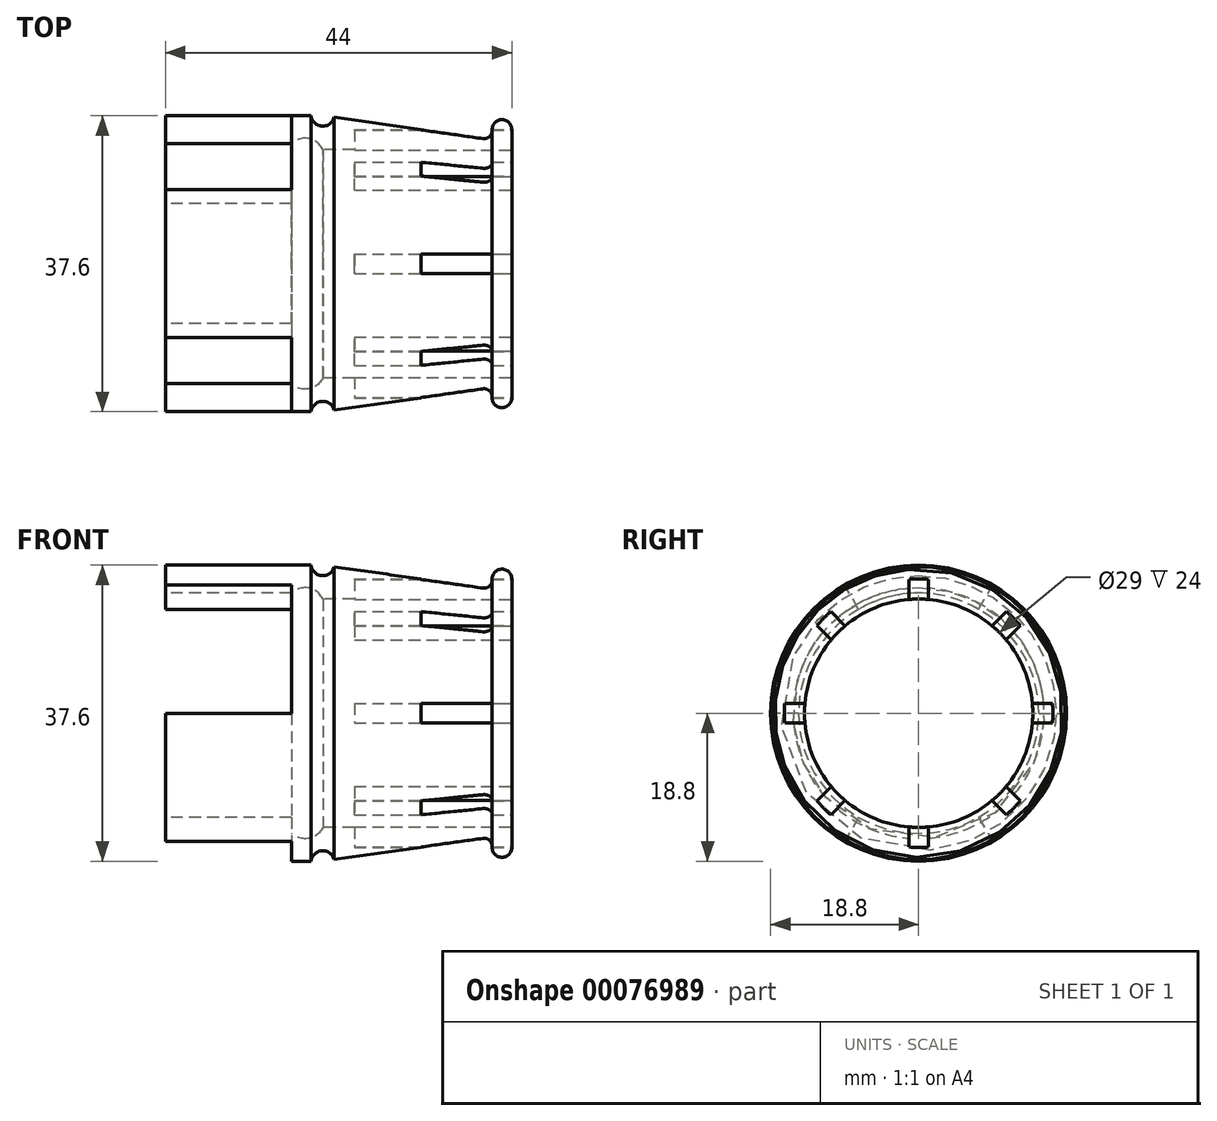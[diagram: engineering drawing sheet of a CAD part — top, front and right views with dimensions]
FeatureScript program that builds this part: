
annotation { "Feature Type Name" : "Feature", "Feature Type Description" : "" }
export const myFeature = defineFeature(function(context is Context, id is Id, definition is map)
    precondition{}
    {
        {
            var Q0;
            Q0=qCreatedBy(makeId("Front.planeOp"),FACE);
            var sketch = newSketch(context, id + "F0", { "sketchPlane" : qUnion([Q0])});
            skLineSegment(sketch, "E0.bottom", {"start": v(0, 14.5) * mm, "end": v(24, 14.5) * mm});
            skLineSegment(sketch, "E0.top", {"start": v(-20, 0) * mm, "end": v(24, 0) * mm});
            skLineSegment(sketch, "E0.left", {"start": v(-20, 14.5) * mm, "end": v(-20, 0) * mm});
            skLineSegment(sketch, "E0.right", {"start": v(24, 14.5) * mm, "end": v(24, 0) * mm});
            skLineSegment(sketch, "E1.top", {"start": v(-20, 18.8) * mm, "end": v(-1.5, 18.8) * mm});
            skLineSegment(sketch, "E1.left", {"start": v(-20, 14.5) * mm, "end": v(-20, 18.8) * mm});
            skLineSegment(sketch, "E1.right", {"start": v(24, 13.25) * mm, "end": v(24, 14.5) * mm});
            skLineSegment(sketch, "E2.bottom", {"start": v(-20, 15.25) * mm, "end": v(-4, 15.25) * mm});
            skLineSegment(sketch, "E2.left", {"start": v(-20, 15.25) * mm, "end": v(-20, 0) * mm});
            skLineSegment(sketch, "E2.right", {"start": v(0, 15.25) * mm, "end": v(0, 0) * mm});
            skLineSegment(sketch, "E3", {"start": v(0, 15.25) * mm, "end": v(0, 14.5) * mm});
            skLineSegment(sketch, "E4", {"start": v(0, 18.8) * mm, "end": v(0, -19.5) * mm, "construction": true});
            skLineSegment(sketch, "E5", {"start": v(1.44, 18.6) * mm, "end": v(20.36, 15.94) * mm});
            skPoint(sketch, "E6.orphan", {"position": v(24, 18.8) * mm});
            skLineSegment(sketch, "E7", {"start": v(-4, 18.8) * mm, "end": v(-4, 0) * mm});
            skLineSegment(sketch, "E8", {"start": v(24, 13.25) * mm, "end": v(24, 17.05) * mm});
            skLineSegment(sketch, "E9", {"start": v(22.75, 18.3) * mm, "end": v(22.75, 18.3) * mm});
            skLineSegment(sketch, "E10", {"start": v(21.5, 17.05) * mm, "end": v(21.5, 16.93) * mm});
            skArc(sketch, "E11.filletArc", {"start": v(20.36, 15.94) * mm, "mid": v(21.16, 16.17) * mm, "end": v(21.5, 16.93) * mm});
            skPoint(sketch, "E12.visualSharp", {"position": v(21.5, 18.3) * mm});
            skArc(sketch, "E12.filletArc", {"start": v(22.75, 18.3) * mm, "mid": v(21.87, 17.93) * mm, "end": v(21.5, 17.05) * mm});
            skPoint(sketch, "E13.visualSharp", {"position": v(24, 18.3) * mm});
            skArc(sketch, "E13.filletArc", {"start": v(24, 17.05) * mm, "mid": v(23.63, 17.93) * mm, "end": v(22.75, 18.3) * mm});
            skArc(sketch, "E14", {"start": v(-1.5, 18.8) * mm, "mid": v(-0.12, 17.48) * mm, "end": v(1.44, 18.6) * mm});
            skPoint(sketch, "E15.orphan", {"position": v(0, -15.25) * mm});
            skArc(sketch, "E16", {"start": v(0, 14.5) * mm, "mid": v(-1.8, 15.9) * mm, "end": v(-4, 15.25) * mm});
            skSolve(sketch);
        }
        {
            var Q0;
            {var subQ0=sQuery(id+"F0.wireOp",EDGE,"E1.left");Q0=makeQuery(id+"F0.imprint","IMPRINT",FACE,{"disambiguationData":[TD([[makeQuery(id+"F0.imprint","IMPRINT",EDGE,{"derivedFrom":subQ0}),-1.0]])]});}
            var Q1;
            {var subQ0=sQuery(id+"F0.wireOp",EDGE,"E1.right");Q1=makeQuery(id+"F0.imprint","IMPRINT",FACE,{"disambiguationData":[TD([[makeQuery(id+"F0.imprint","IMPRINT",EDGE,{"derivedFrom":subQ0}),1.0]])]});}
            var Q2;
            Q2=makeQuery(id+"F0.imprint","IMPRINT",FACE,{"disambiguationData":[TD([[makeQuery(id+"F0.imprint","IMPRINT",EDGE,{"derivedFrom":sQuery(id+"F0.wireOp",EDGE,"E5")}),-1.0]])]});
            var Q3;
            Q3=sQuery(id+"F0.wireOp",EDGE,"E0.top");
            revolve(context, id + "F1", {"entities" : qUnion([Q0, Q1, Q2]), "axis" : qUnion([Q3]), "revolveType" : RevolveType.FULL});
        }
        {
            var Q0;
            Q0=makeQuery(id+"F1.opRevolve","SWEPT_FACE",FACE,{"disambiguationData":[OSD([sQuery(id+"F0.wireOp",EDGE,"E1.left")])]});
            var sketch = newSketch(context, id + "F2", { "sketchPlane" : qUnion([Q0])});
            skCircle(sketch, "E17.0", {"center": v(0, 0) * mm, "radius": 15.25 * mm});
            skCircle(sketch, "E18.0", {"center": v(0, 0) * mm, "radius": 18.8 * mm});
            skLineSegment(sketch, "E19", {"start": v(0, 0) * mm, "end": v(-9.4, 16.28) * mm});
            skLineSegment(sketch, "E20", {"start": v(0, 0) * mm, "end": v(-18.8, 0) * mm});
            skLineSegment(sketch, "E21", {"start": v(0, 0) * mm, "end": v(9.4, 16.28) * mm});
            skLineSegment(sketch, "E22", {"start": v(0, 0) * mm, "end": v(18.8, 0) * mm});
            skLineSegment(sketch, "E23", {"start": v(0, 0) * mm, "end": v(9.4, -16.28) * mm});
            skLineSegment(sketch, "E24", {"start": v(0, 0) * mm, "end": v(-9.4, -16.28) * mm});
            skSolve(sketch);
        }
        {
            var Q0;
            {var subQ0=sQuery(id+"F2.wireOp",EDGE,"E20");var subQ1=sQuery(id+"F2.wireOp",EDGE,"E17.0");var subQ2=makeQuery(id+"F2.imprint","INTERSECT",VERTEX,{"derivedFrom":[subQ1,subQ0]});Q0=makeQuery(id+"F2.imprint","IMPRINT",FACE,{"disambiguationData":[TD([[makeQuery(id+"F2.imprint","IMPRINT",EDGE,{"disambiguationData":[TD([[subQ2,1.0]])],"derivedFrom":subQ1}),-1.0]])]});}
            var Q1;
            {var subQ0=sQuery(id+"F2.wireOp",EDGE,"E22");var subQ1=sQuery(id+"F2.wireOp",EDGE,"E17.0");var subQ2=makeQuery(id+"F2.imprint","INTERSECT",VERTEX,{"derivedFrom":[subQ1,subQ0]});Q1=makeQuery(id+"F2.imprint","IMPRINT",FACE,{"disambiguationData":[TD([[makeQuery(id+"F2.imprint","IMPRINT",EDGE,{"disambiguationData":[TD([[subQ2,-1.0]])],"derivedFrom":subQ1}),-1.0]])]});}
            var Q2;
            {var subQ0=sQuery(id+"F2.wireOp",EDGE,"E24");var subQ1=sQuery(id+"F2.wireOp",EDGE,"E17.0");var subQ2=makeQuery(id+"F2.imprint","INTERSECT",VERTEX,{"derivedFrom":[subQ1,subQ0]});Q2=makeQuery(id+"F2.imprint","IMPRINT",FACE,{"disambiguationData":[TD([[makeQuery(id+"F2.imprint","IMPRINT",EDGE,{"disambiguationData":[TD([[subQ2,-1.0]])],"derivedFrom":subQ1}),-1.0]])]});}
            extrude(context, id + "F3", {"entities" : qUnion([Q0, Q1, Q2]), "operationType" : NewBodyOperationType.REMOVE, "oppositeDirection" : true, "depth" : 16 * mm});
        }
        {
            var Q0;
            Q0=makeQuery(id+"F1.opRevolve","SWEPT_FACE",FACE,{"disambiguationData":[OSD([sQuery(id+"F0.wireOp",EDGE,"E8")])]});
            var sketch = newSketch(context, id + "F4", { "sketchPlane" : qUnion([Q0])});
            skCircle(sketch, "E25.0", {"center": v(0, 0) * mm, "radius": 14.5 * mm, "construction": true});
            skCircle(sketch, "E26.0", {"center": v(0, 0) * mm, "radius": 17.05 * mm, "construction": true});
            skCircle(sketch, "E27.0", {"center": v(0, 0) * mm, "radius": 18.8 * mm, "construction": true});
            skLineSegment(sketch, "E28", {"start": v(0, 21) * mm, "end": v(0, -20.6) * mm, "construction": true});
            skLineSegment(sketch, "E29", {"start": v(22.7, 0) * mm, "end": v(-23.6, 0) * mm, "construction": true});
            skLineSegment(sketch, "E30", {"start": v(-17.5, 17.5) * mm, "end": v(0, 0) * mm, "construction": true});
            skLineSegment(sketch, "E31", {"start": v(0, 0) * mm, "end": v(17.06, -17.06) * mm, "construction": true});
            skLineSegment(sketch, "E32", {"start": v(0, 0) * mm, "end": v(14.47, 14.47) * mm, "construction": true});
            skLineSegment(sketch, "E33", {"start": v(0, 0) * mm, "end": v(-15.58, -15.58) * mm, "construction": true});
            skArc(sketch, "E34.0.startCap", {"start": v(-18.39, 16.62) * mm, "mid": v(-18.39, 18.39) * mm, "end": v(-16.62, 18.39) * mm});
            skArc(sketch, "E34.0.endCap", {"start": v(0.88, 0.88) * mm, "mid": v(0.88, -0.88) * mm, "end": v(-0.88, -0.88) * mm});
            skLineSegment(sketch, "E34.0.left", {"start": v(-16.62, 18.39) * mm, "end": v(0.88, 0.88) * mm});
            skLineSegment(sketch, "E34.0.right", {"start": v(-18.39, 16.62) * mm, "end": v(-0.88, -0.88) * mm});
            skArc(sketch, "E35.0.startCap", {"start": v(-1.25, 21) * mm, "mid": v(0, 22.25) * mm, "end": v(1.25, 21) * mm});
            skArc(sketch, "E35.0.endCap", {"start": v(1.25, -20.6) * mm, "mid": v(0, -21.85) * mm, "end": v(-1.25, -20.6) * mm});
            skLineSegment(sketch, "E35.0.left", {"start": v(1.25, 21) * mm, "end": v(1.25, -20.6) * mm});
            skLineSegment(sketch, "E35.0.right", {"start": v(-1.25, 21) * mm, "end": v(-1.25, -20.6) * mm});
            skArc(sketch, "E36.0.startCap", {"start": v(0.88, -0.88) * mm, "mid": v(-0.88, -0.88) * mm, "end": v(-0.88, 0.88) * mm});
            skArc(sketch, "E36.0.endCap", {"start": v(13.58, 15.35) * mm, "mid": v(15.35, 15.35) * mm, "end": v(15.35, 13.58) * mm});
            skLineSegment(sketch, "E36.0.left", {"start": v(-0.88, 0.88) * mm, "end": v(13.58, 15.35) * mm});
            skLineSegment(sketch, "E36.0.right", {"start": v(0.88, -0.88) * mm, "end": v(15.35, 13.58) * mm});
            skArc(sketch, "E36.1.startCap", {"start": v(-0.88, 0.88) * mm, "mid": v(0.88, 0.88) * mm, "end": v(0.88, -0.88) * mm});
            skArc(sketch, "E36.1.endCap", {"start": v(-14.7, -16.46) * mm, "mid": v(-16.46, -16.46) * mm, "end": v(-16.46, -14.7) * mm});
            skLineSegment(sketch, "E36.1.left", {"start": v(0.88, -0.88) * mm, "end": v(-14.7, -16.46) * mm});
            skLineSegment(sketch, "E36.1.right", {"start": v(-0.88, 0.88) * mm, "end": v(-16.46, -14.7) * mm});
            skArc(sketch, "E36.2.startCap", {"start": v(22.7, 1.25) * mm, "mid": v(23.96, 0) * mm, "end": v(22.7, -1.25) * mm});
            skArc(sketch, "E36.2.endCap", {"start": v(-23.6, -1.25) * mm, "mid": v(-24.84, 0) * mm, "end": v(-23.6, 1.25) * mm});
            skLineSegment(sketch, "E36.2.left", {"start": v(22.7, -1.25) * mm, "end": v(-23.6, -1.25) * mm});
            skLineSegment(sketch, "E36.2.right", {"start": v(22.7, 1.25) * mm, "end": v(-23.6, 1.25) * mm});
            skArc(sketch, "E36.3.startCap", {"start": v(-0.88, -0.88) * mm, "mid": v(-0.88, 0.88) * mm, "end": v(0.88, 0.88) * mm});
            skArc(sketch, "E36.3.endCap", {"start": v(17.95, -16.18) * mm, "mid": v(17.95, -17.95) * mm, "end": v(16.18, -17.95) * mm});
            skLineSegment(sketch, "E36.3.left", {"start": v(0.88, 0.88) * mm, "end": v(17.95, -16.18) * mm});
            skLineSegment(sketch, "E36.3.right", {"start": v(-0.88, -0.88) * mm, "end": v(16.18, -17.95) * mm});
            skSolve(sketch);
        }
        {
            var Q0;
            {var subQ0=sQuery(id+"F4.wireOp",EDGE,"E34.0.left");var subQ1=sQuery(id+"F0.wireOp",EDGE,"E8");var subQ2=makeQuery(id+"F1.opRevolve","SWEPT_EDGE",EDGE,{"disambiguationData":[OSD([subQ1,sQuery(id+"F0.wireOp",EDGE,"E13.filletArc")])]});var subQ3=makeQuery(id+"F4.imprint","INTERSECT",VERTEX,{"derivedFrom":[subQ2,subQ0]});Q0=makeQuery(id+"F4.imprint","IMPRINT",FACE,{"disambiguationData":[TD([[makeQuery(id+"F4.imprint","IMPRINT",EDGE,{"disambiguationData":[TD([[subQ3,-1.0]])],"derivedFrom":subQ0}),-1.0]])]});}
            var Q1;
            {var subQ0=sQuery(id+"F4.wireOp",EDGE,"E34.0.startCap");Q1=makeQuery(id+"F4.imprint","IMPRINT",FACE,{"disambiguationData":[TD([[makeQuery(id+"F4.imprint","IMPRINT",EDGE,{"derivedFrom":subQ0}),-1.0]])]});}
            var Q2;
            {var subQ0=sQuery(id+"F4.wireOp",EDGE,"E35.0.left");var subQ1=sQuery(id+"F0.wireOp",EDGE,"E8");var subQ2=makeQuery(id+"F1.opRevolve","SWEPT_EDGE",EDGE,{"disambiguationData":[OSD([subQ1,sQuery(id+"F0.wireOp",EDGE,"E13.filletArc")])]});var subQ3=makeQuery(id+"F4.imprint","INTERSECT",VERTEX,{"disambiguationData":[OD(0.0)],"derivedFrom":[subQ2,subQ0]});Q2=makeQuery(id+"F4.imprint","IMPRINT",FACE,{"disambiguationData":[TD([[makeQuery(id+"F4.imprint","IMPRINT",EDGE,{"disambiguationData":[TD([[subQ3,-1.0]])],"derivedFrom":subQ0}),-1.0]])]});}
            var Q3;
            {var subQ0=sQuery(id+"F4.wireOp",EDGE,"E35.0.startCap");Q3=makeQuery(id+"F4.imprint","IMPRINT",FACE,{"disambiguationData":[TD([[makeQuery(id+"F4.imprint","IMPRINT",EDGE,{"derivedFrom":subQ0}),-1.0]])]});}
            var Q4;
            {var subQ0=sQuery(id+"F4.wireOp",EDGE,"E36.0.left");var subQ1=sQuery(id+"F0.wireOp",EDGE,"E8");var subQ2=makeQuery(id+"F1.opRevolve","SWEPT_EDGE",EDGE,{"disambiguationData":[OSD([subQ1,sQuery(id+"F0.wireOp",EDGE,"E13.filletArc")])]});var subQ3=makeQuery(id+"F4.imprint","INTERSECT",VERTEX,{"derivedFrom":[subQ2,subQ0]});Q4=makeQuery(id+"F4.imprint","IMPRINT",FACE,{"disambiguationData":[TD([[makeQuery(id+"F4.imprint","IMPRINT",EDGE,{"disambiguationData":[TD([[subQ3,1.0]])],"derivedFrom":subQ0}),-1.0]])]});}
            var Q5;
            {var subQ0=sQuery(id+"F4.wireOp",EDGE,"E36.0.endCap");Q5=makeQuery(id+"F4.imprint","IMPRINT",FACE,{"disambiguationData":[TD([[makeQuery(id+"F4.imprint","IMPRINT",EDGE,{"derivedFrom":subQ0}),-1.0]])]});}
            var Q6;
            {var subQ0=sQuery(id+"F4.wireOp",EDGE,"E36.2.left");var subQ1=sQuery(id+"F0.wireOp",EDGE,"E8");var subQ2=makeQuery(id+"F1.opRevolve","SWEPT_EDGE",EDGE,{"disambiguationData":[OSD([subQ1,sQuery(id+"F0.wireOp",EDGE,"E13.filletArc")])]});var subQ3=makeQuery(id+"F4.imprint","INTERSECT",VERTEX,{"disambiguationData":[OD(0.0)],"derivedFrom":[subQ2,subQ0]});Q6=makeQuery(id+"F4.imprint","IMPRINT",FACE,{"disambiguationData":[TD([[makeQuery(id+"F4.imprint","IMPRINT",EDGE,{"disambiguationData":[TD([[subQ3,-1.0]])],"derivedFrom":subQ0}),-1.0]])]});}
            var Q7;
            {var subQ0=sQuery(id+"F4.wireOp",EDGE,"E36.2.startCap");Q7=makeQuery(id+"F4.imprint","IMPRINT",FACE,{"disambiguationData":[TD([[makeQuery(id+"F4.imprint","IMPRINT",EDGE,{"derivedFrom":subQ0}),-1.0]])]});}
            var Q8;
            {var subQ0=sQuery(id+"F4.wireOp",EDGE,"E36.3.left");var subQ1=sQuery(id+"F0.wireOp",EDGE,"E8");var subQ2=makeQuery(id+"F1.opRevolve","SWEPT_EDGE",EDGE,{"disambiguationData":[OSD([subQ1,sQuery(id+"F0.wireOp",EDGE,"E13.filletArc")])]});var subQ3=makeQuery(id+"F4.imprint","INTERSECT",VERTEX,{"derivedFrom":[subQ2,subQ0]});Q8=makeQuery(id+"F4.imprint","IMPRINT",FACE,{"disambiguationData":[TD([[makeQuery(id+"F4.imprint","IMPRINT",EDGE,{"disambiguationData":[TD([[subQ3,1.0]])],"derivedFrom":subQ0}),-1.0]])]});}
            var Q9;
            {var subQ0=sQuery(id+"F4.wireOp",EDGE,"E36.3.endCap");Q9=makeQuery(id+"F4.imprint","IMPRINT",FACE,{"disambiguationData":[TD([[makeQuery(id+"F4.imprint","IMPRINT",EDGE,{"derivedFrom":subQ0}),-1.0]])]});}
            var Q10;
            {var subQ0=sQuery(id+"F4.wireOp",EDGE,"E35.0.left");var subQ1=sQuery(id+"F0.wireOp",EDGE,"E8");var subQ2=makeQuery(id+"F1.opRevolve","SWEPT_EDGE",EDGE,{"disambiguationData":[OSD([subQ1,sQuery(id+"F0.wireOp",EDGE,"E13.filletArc")])]});var subQ3=makeQuery(id+"F4.imprint","INTERSECT",VERTEX,{"disambiguationData":[OD(1.0)],"derivedFrom":[subQ2,subQ0]});Q10=makeQuery(id+"F4.imprint","IMPRINT",FACE,{"disambiguationData":[TD([[makeQuery(id+"F4.imprint","IMPRINT",EDGE,{"disambiguationData":[TD([[subQ3,1.0]])],"derivedFrom":subQ0}),-1.0]])]});}
            var Q11;
            {var subQ0=sQuery(id+"F4.wireOp",EDGE,"E35.0.endCap");Q11=makeQuery(id+"F4.imprint","IMPRINT",FACE,{"disambiguationData":[TD([[makeQuery(id+"F4.imprint","IMPRINT",EDGE,{"derivedFrom":subQ0}),-1.0]])]});}
            var Q12;
            {var subQ0=sQuery(id+"F4.wireOp",EDGE,"E36.1.left");var subQ1=sQuery(id+"F0.wireOp",EDGE,"E8");var subQ2=makeQuery(id+"F1.opRevolve","SWEPT_EDGE",EDGE,{"disambiguationData":[OSD([subQ1,sQuery(id+"F0.wireOp",EDGE,"E13.filletArc")])]});var subQ3=makeQuery(id+"F4.imprint","INTERSECT",VERTEX,{"derivedFrom":[subQ2,subQ0]});Q12=makeQuery(id+"F4.imprint","IMPRINT",FACE,{"disambiguationData":[TD([[makeQuery(id+"F4.imprint","IMPRINT",EDGE,{"disambiguationData":[TD([[subQ3,1.0]])],"derivedFrom":subQ0}),-1.0]])]});}
            var Q13;
            {var subQ0=sQuery(id+"F4.wireOp",EDGE,"E36.1.endCap");Q13=makeQuery(id+"F4.imprint","IMPRINT",FACE,{"disambiguationData":[TD([[makeQuery(id+"F4.imprint","IMPRINT",EDGE,{"derivedFrom":subQ0}),-1.0]])]});}
            var Q14;
            {var subQ0=sQuery(id+"F4.wireOp",EDGE,"E36.2.left");var subQ1=sQuery(id+"F0.wireOp",EDGE,"E8");var subQ2=makeQuery(id+"F1.opRevolve","SWEPT_EDGE",EDGE,{"disambiguationData":[OSD([subQ1,sQuery(id+"F0.wireOp",EDGE,"E13.filletArc")])]});var subQ3=makeQuery(id+"F4.imprint","INTERSECT",VERTEX,{"disambiguationData":[OD(1.0)],"derivedFrom":[subQ2,subQ0]});Q14=makeQuery(id+"F4.imprint","IMPRINT",FACE,{"disambiguationData":[TD([[makeQuery(id+"F4.imprint","IMPRINT",EDGE,{"disambiguationData":[TD([[subQ3,1.0]])],"derivedFrom":subQ0}),-1.0]])]});}
            var Q15;
            {var subQ0=sQuery(id+"F4.wireOp",EDGE,"E36.2.endCap");Q15=makeQuery(id+"F4.imprint","IMPRINT",FACE,{"disambiguationData":[TD([[makeQuery(id+"F4.imprint","IMPRINT",EDGE,{"derivedFrom":subQ0}),-1.0]])]});}
            extrude(context, id + "F5", {"entities" : qUnion([Q0, Q1, Q2, Q3, Q4, Q5, Q6, Q7, Q8, Q9, Q10, Q11, Q12, Q13, Q14, Q15]), "operationType" : NewBodyOperationType.REMOVE, "oppositeDirection" : true, "depth" : 20 * mm});
        }
    });
